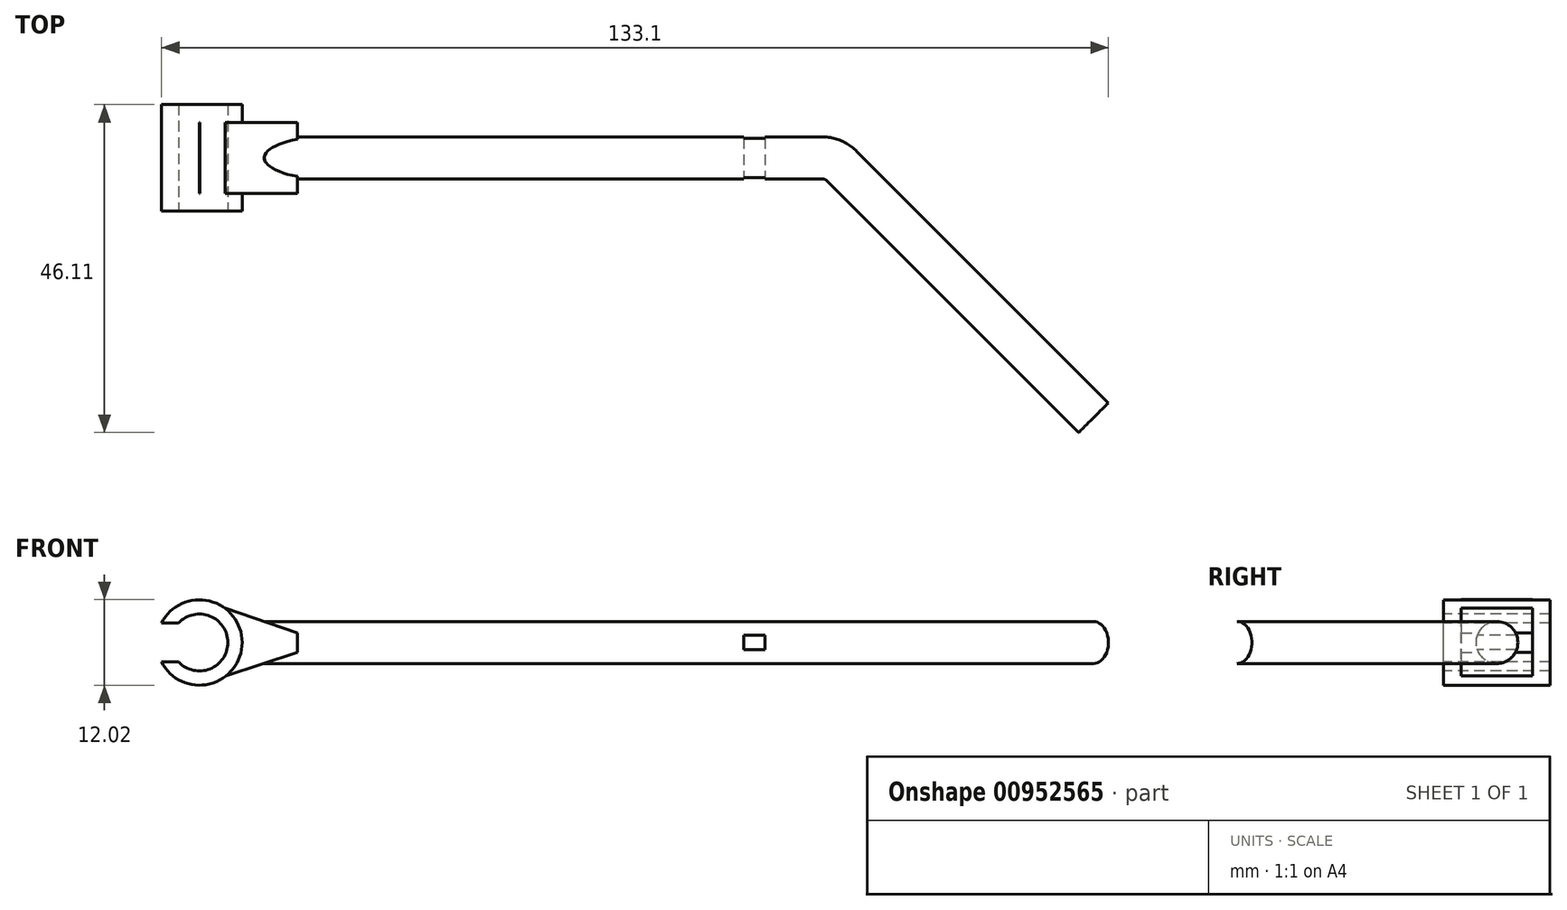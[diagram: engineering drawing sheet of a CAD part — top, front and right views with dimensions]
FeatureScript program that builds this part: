
annotation { "Feature Type Name" : "Feature", "Feature Type Description" : "" }
export const myFeature = defineFeature(function(context is Context, id is Id, definition is map)
    precondition{}
    {
        {
            var Q0;
            Q0=qCreatedBy(makeId("Front.planeOp"),FACE);
            var sketch = newSketch(context, id + "F0", { "sketchPlane" : qUnion([Q0])});
            skCircle(sketch, "E0", {"center": v(0, 0) * mm, "radius": 4 * mm});
            skCircle(sketch, "E1", {"center": v(0, 0) * mm, "radius": 6 * mm});
            skSolve(sketch);
        }
        {
            var Q0;
            Q0=qSketchRegion(id+"F0",true);
            extrude(context, id + "F1", {"entities" : qUnion([Q0]), "endBound" : BoundingType.SYMMETRIC, "oppositeDirection" : true, "depth" : 15 * mm, "offsetDistance" : 25 * mm});
        }
        {
            var Q0;
            Q0=qCreatedBy(makeId("Right.planeOp"),FACE);
            cPlane(context, id + "F2", {"entities" : qUnion([Q0]), "cplaneType" : CPlaneType.OFFSET, "offset" : 4.5 * mm, "width" : 150 * mm, "height" : 150 * mm});
        }
        {
            var Q0;
            Q0=qCreatedBy(id+"F2.planeOp",FACE);
            var sketch = newSketch(context, id + "F3", { "sketchPlane" : qUnion([Q0])});
            skCircle(sketch, "E2", {"center": v(0, 0) * mm, "radius": 2.95 * mm});
            skSolve(sketch);
        }
        {
            var Q0;
            Q0=qSketchRegion(id+"F3",true);
            extrude(context, id + "F4", {"entities" : qUnion([Q0]), "operationType" : NewBodyOperationType.ADD, "depth" : 80 * mm, "offsetDistance" : 25 * mm});
        }
        {
            var Q0;
            Q0=makeQuery(id+"F1.opExtrude","CAP_FACE",FACE,{"disambiguationData":[OSD([sQuery(id+"F0.wireOp",EDGE,"E0"),sQuery(id+"F0.wireOp",EDGE,"E1")])],"isStart":true});
            var sketch = newSketch(context, id + "F5", { "sketchPlane" : qUnion([Q0])});
            skLineSegment(sketch, "E3.bottom", {"start": v(-20, 2.75) * mm, "end": v(0, 2.75) * mm});
            skLineSegment(sketch, "E3.top", {"start": v(-20, -2.75) * mm, "end": v(0, -2.75) * mm});
            skLineSegment(sketch, "E3.left", {"start": v(-20, 2.75) * mm, "end": v(-20, -2.75) * mm});
            skLineSegment(sketch, "E3.right", {"start": v(0, 2.75) * mm, "end": v(0, -2.75) * mm});
            skPoint(sketch, "E4", {"position": v(-20, 0) * mm});
            skSolve(sketch);
        }
        {
            var Q0;
            Q0=qSketchRegion(id+"F5",true);
            extrude(context, id + "F6", {"entities" : qUnion([Q0]), "operationType" : NewBodyOperationType.REMOVE, "oppositeDirection" : true, "depth" : 25 * mm, "offsetDistance" : 25 * mm});
        }
        {
            var Q0;
            Q0=qCreatedBy(id+"F2.planeOp",FACE);
            cPlane(context, id + "F7", {"entities" : qUnion([Q0]), "cplaneType" : CPlaneType.OFFSET, "offset" : 12 * mm, "width" : 150 * mm, "height" : 150 * mm});
        }
        {
            var Q0;
            Q0=qCreatedBy(id+"F7.planeOp",FACE);
            var sketch = newSketch(context, id + "F8", { "sketchPlane" : qUnion([Q0])});
            skLineSegment(sketch, "E5", {"start": v(-2.5, 0) * mm, "end": v(2.5, 0) * mm, "construction": true});
            skPoint(sketch, "E6", {"position": v(0, 0) * mm});
            skArc(sketch, "E7", {"start": v(3.5, 0) * mm, "mid": v(2.5, 1) * mm, "end": v(1.5, 0) * mm});
            skLineSegment(sketch, "E8", {"start": v(0, 0) * mm, "end": v(0, -1.96) * mm, "construction": true});
            skArc(sketch, "E9.MirrorCS", {"start": v(-3.5, 0) * mm, "mid": v(-2.5, 1) * mm, "end": v(-1.5, 0) * mm});
            skSolve(sketch);
        }
        {
            var Q0;
            Q0=qCreatedBy(id+"F7.planeOp",FACE);
            var sketch = newSketch(context, id + "F9", { "sketchPlane" : qUnion([Q0])});
            skLineSegment(sketch, "E10", {"start": v(-4.04, 0) * mm, "end": v(4.97, 0) * mm, "construction": true});
            skSolve(sketch);
        }
        {
            var Q0;
            Q0=makeQuery(id+"F4.opExtrude","CAP_FACE",FACE,{"disambiguationData":[OSD([sQuery(id+"F3.wireOp",EDGE,"E2")])],"isStart":false});
            var sketch = newSketch(context, id + "F10", { "sketchPlane" : qUnion([Q0])});
            skCircle(sketch, "E11", {"center": v(0, 0) * mm, "radius": 2.5 * mm});
            skSolve(sketch);
        }
        {
            var Q0;
            Q0=makeQuery(id+"F0.imprint","IMPRINT",FACE,{"disambiguationData":[TD([[makeQuery(id+"F0.imprint","IMPRINT",EDGE,{"derivedFrom":sQuery(id+"F0.wireOp",EDGE,"E0")}),1.0]])]});
            var sketch = newSketch(context, id + "F11", { "sketchPlane" : qUnion([Q0])});
            skLineSegment(sketch, "E12", {"start": v(0, 6.02) * mm, "end": v(13.77, 1.37) * mm});
            skLineSegment(sketch, "E13", {"start": v(13.77, 1.37) * mm, "end": v(13.77, -1.38) * mm});
            skLineSegment(sketch, "E14", {"start": v(13.77, -1.38) * mm, "end": v(0, -5.9) * mm});
            skLineSegment(sketch, "E15", {"start": v(0, -5.9) * mm, "end": v(5.86, 0) * mm});
            skLineSegment(sketch, "E16", {"start": v(5.86, 0) * mm, "end": v(0, 6.02) * mm});
            skSolve(sketch);
        }
        {
            var Q0;
            Q0 = qSketchRegion(id + "F11", true);
            extrude(context, id + "F12", {"entities" : qUnion([Q0]), "operationType" : NewBodyOperationType.ADD, "endBound" : BoundingType.SYMMETRIC, "depth" : 10 * mm, "offsetDistance" : 25 * mm});
        }
        {
            var Q0;
            Q0=qCreatedBy(makeId("Front.planeOp"),FACE);
            var sketch = newSketch(context, id + "F13", { "sketchPlane" : qUnion([Q0])});
            skLineSegment(sketch, "E17.bottom", {"start": v(79.5, 1) * mm, "end": v(76.5, 1) * mm});
            skLineSegment(sketch, "E17.top", {"start": v(79.5, -1) * mm, "end": v(76.5, -1) * mm});
            skLineSegment(sketch, "E17.left", {"start": v(79.5, 1) * mm, "end": v(79.5, -1) * mm});
            skLineSegment(sketch, "E17.right", {"start": v(76.5, 1) * mm, "end": v(76.5, -1) * mm});
            skPoint(sketch, "E18", {"position": v(79.5, 0) * mm});
            skPoint(sketch, "E19", {"position": v(84.5, 0) * mm});
            skSolve(sketch);
        }
        {
            var Q0;
            Q0 = qSketchRegion(id + "F13", true);
            extrude(context, id + "F14", {"entities" : qUnion([Q0]), "operationType" : NewBodyOperationType.REMOVE, "endBound" : BoundingType.SYMMETRIC, "oppositeDirection" : true, "depth" : 25 * mm, "offsetDistance" : 25 * mm});
        }
        {
            var Q0;
            Q0=qCreatedBy(makeId("Top.planeOp"),FACE);
            var sketch = newSketch(context, id + "F15", { "sketchPlane" : qUnion([Q0])});
            skLineSegment(sketch, "E20", {"start": v(84.5, 0) * mm, "end": v(87.5, 0) * mm});
            skLineSegment(sketch, "E21", {"start": v(91.5, -4) * mm, "end": v(91.5, -7) * mm, "construction": true});
            skPoint(sketch, "E22.visualSharp", {"position": v(91.5, 0) * mm});
            skArc(sketch, "E22.filletArc", {"start": v(91.5, -4) * mm, "mid": v(91.2, -2.47) * mm, "end": v(90.33, -1.17) * mm, "construction": true});
            skLineSegment(sketch, "E23", {"start": v(91.5, 0) * mm, "end": v(87.5, -4) * mm, "construction": true});
            skArc(sketch, "E24", {"start": v(90.33, -1.17) * mm, "mid": v(89.03, -0.3) * mm, "end": v(87.5, 0) * mm});
            skLineSegment(sketch, "E25", {"start": v(90.33, -1.17) * mm, "end": v(125.68, -36.53) * mm});
            skSolve(sketch);
        }
        {
            var Q0;
            Q0=makeQuery(id+"F10.imprint","IMPRINT",FACE,{"disambiguationData":[TD([[makeQuery(id+"F10.imprint","IMPRINT",EDGE,{"derivedFrom":sQuery(id+"F10.wireOp",EDGE,"E11")}),1.0]])]});
            var sketch = newSketch(context, id + "F16", { "sketchPlane" : qUnion([Q0])});
            skCircle(sketch, "E26", {"center": v(0, 0) * mm, "radius": 2.95 * mm});
            skSolve(sketch);
        }
        {
            var Q0;
            Q0 = qSketchRegion(id + "F16", true);
            var Q1;
            Q1=sQuery(id+"F15.wireOp",EDGE,"E20");
            var Q2;
            Q2=sQuery(id+"F15.wireOp",EDGE,"E24");
            var Q3;
            Q3=sQuery(id+"F15.wireOp",EDGE,"E25");
            sweep(context, id + "F17", {"operationType" : NewBodyOperationType.ADD, "profiles" : qUnion([Q0]), "path" : qUnion([Q1, Q2, Q3])});
        }
    });
